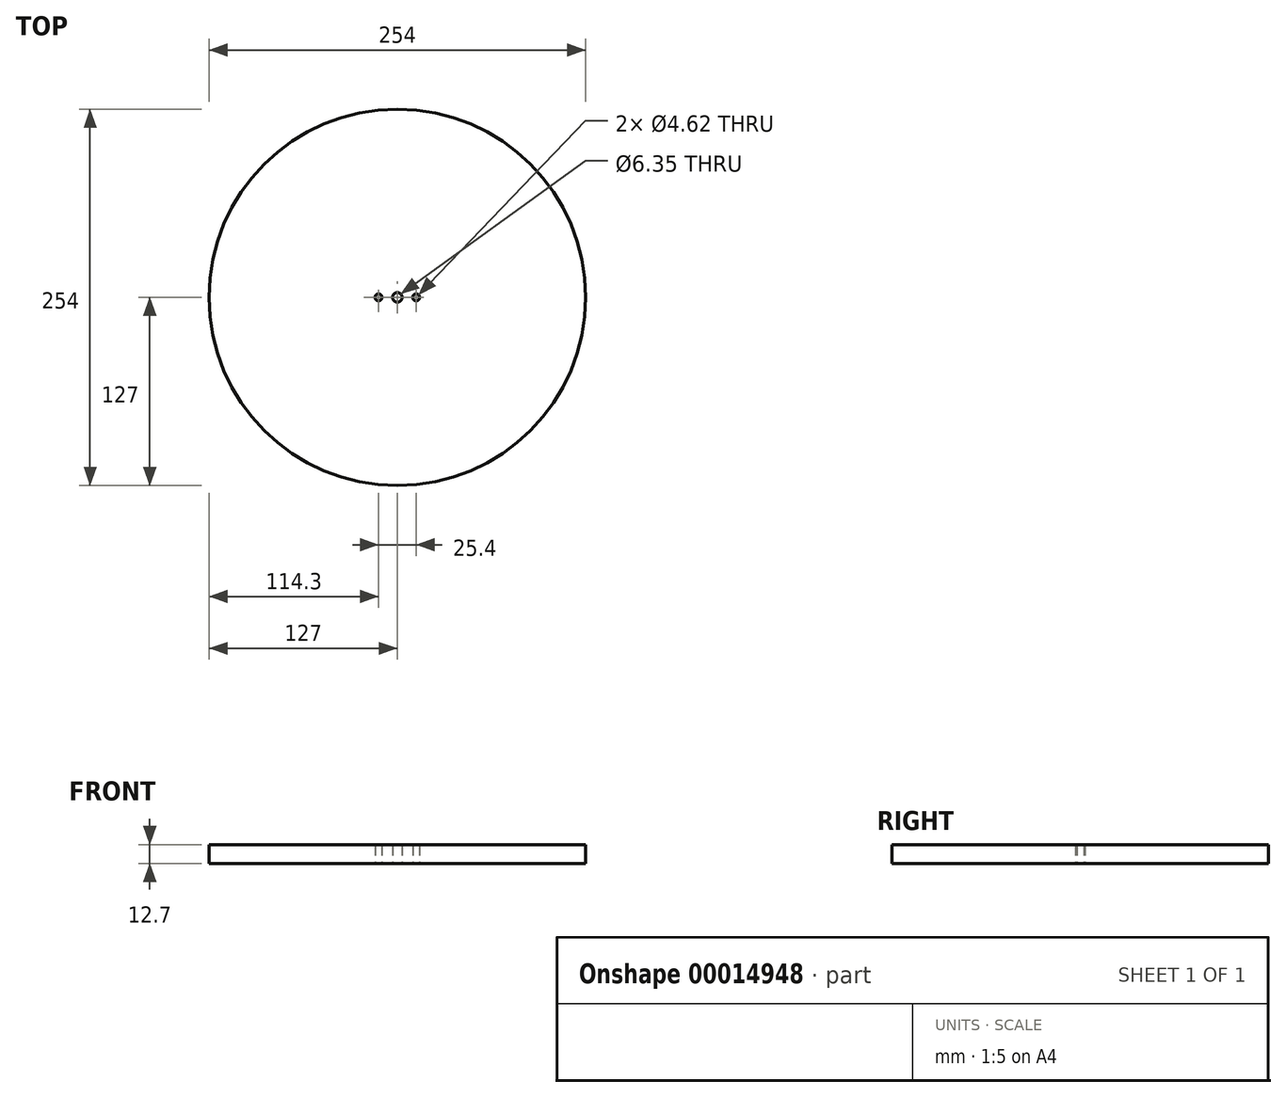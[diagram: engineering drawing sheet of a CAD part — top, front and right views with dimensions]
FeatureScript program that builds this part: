
annotation { "Feature Type Name" : "Feature", "Feature Type Description" : "" }
export const myFeature = defineFeature(function(context is Context, id is Id, definition is map)
    precondition{}
    {
        {
            var Q0;
            Q0=qCreatedBy(makeId("Top.planeOp"),FACE);
            var sketch = newSketch(context, id + "F0", { "sketchPlane" : qUnion([Q0])});
            skCircle(sketch, "E0", {"center": v(0, 0) * mm, "radius": 127 * mm});
            skCircle(sketch, "E1", {"center": v(0, 0) * mm, "radius": 3.18 * mm});
            skCircle(sketch, "E2", {"center": v(-12.7, 0) * mm, "radius": 2.31 * mm});
            skCircle(sketch, "E3", {"center": v(12.7, 0) * mm, "radius": 2.31 * mm});
            skSolve(sketch);
        }
        {
            var Q0;
            Q0=makeQuery(id+"F0.imprint","IMPRINT",FACE,{"disambiguationData":[TD([[makeQuery(id+"F0.imprint","IMPRINT",EDGE,{"derivedFrom":sQuery(id+"F0.wireOp",EDGE,"E0")}),1.0]])]});
            extrude(context, id + "F1", {"entities" : qUnion([Q0]), "depth" : 12.7 * mm});
        }
    });
